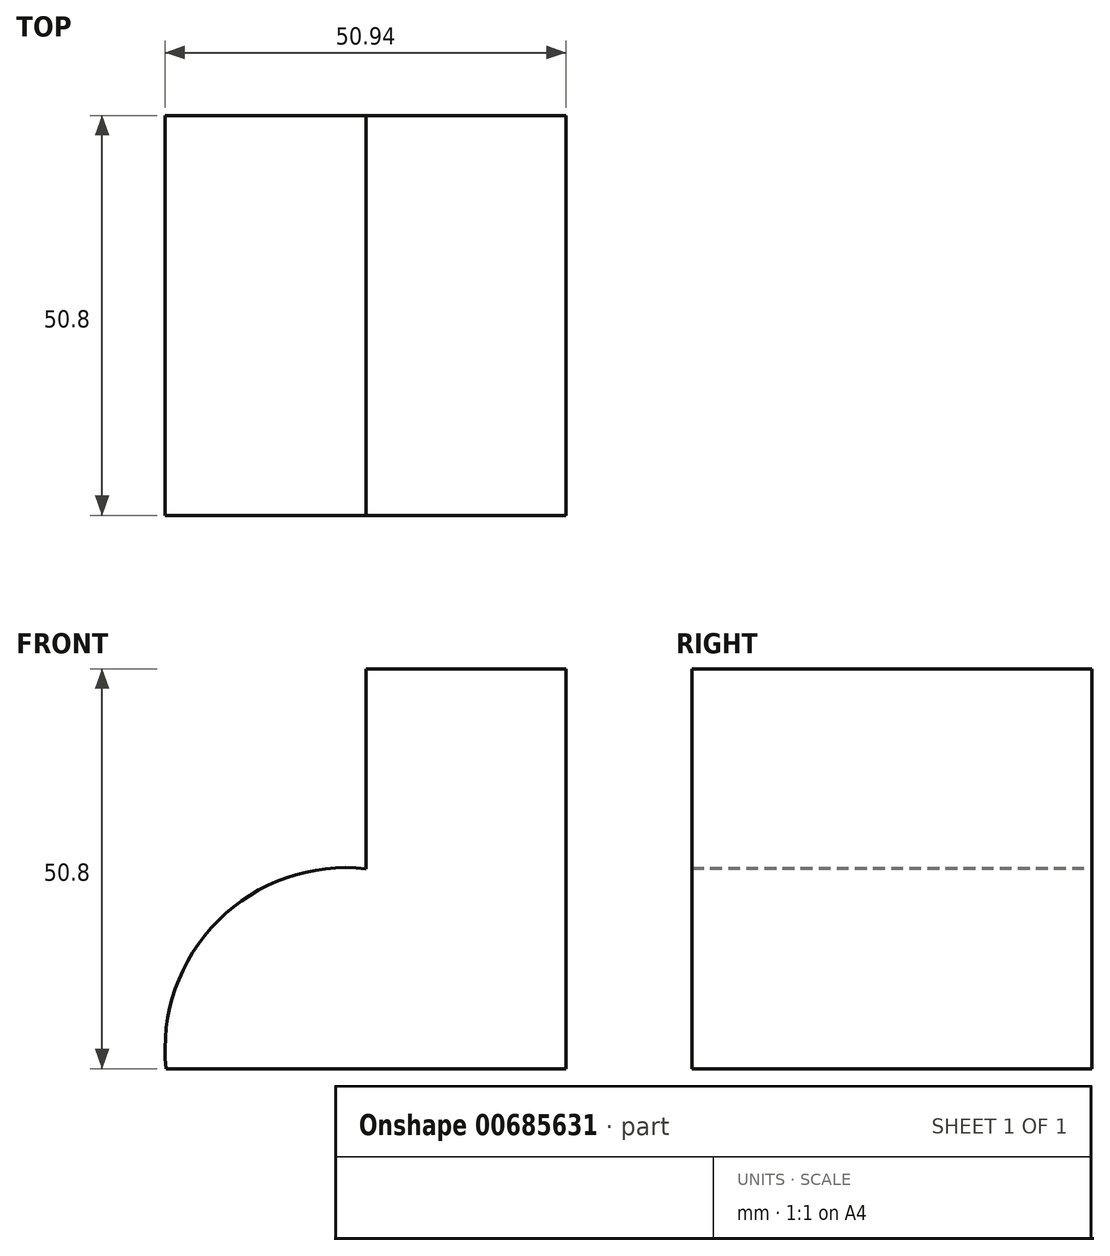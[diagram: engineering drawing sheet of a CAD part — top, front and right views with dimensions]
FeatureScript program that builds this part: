
annotation { "Feature Type Name" : "Feature", "Feature Type Description" : "" }
export const myFeature = defineFeature(function(context is Context, id is Id, definition is map)
    precondition{}
    {
        {
            var Q0;
            Q0=qCreatedBy(makeId("Front.planeOp"),FACE);
            var sketch = newSketch(context, id + "F0", { "sketchPlane" : qUnion([Q0])});
            skLineSegment(sketch, "E0", {"start": v(36.72, 23.26) * mm, "end": v(36.72, -27.54) * mm});
            skLineSegment(sketch, "E1", {"start": v(36.72, -27.54) * mm, "end": v(-14.08, -27.54) * mm});
            skLineSegment(sketch, "E2", {"start": v(36.72, 23.26) * mm, "end": v(11.32, 23.26) * mm});
            skLineSegment(sketch, "E3", {"start": v(11.32, 23.26) * mm, "end": v(11.32, -2.14) * mm});
            skArc(sketch, "E4", {"start": v(11.32, -2.14) * mm, "mid": v(-7.48, -8.74) * mm, "end": v(-14.08, -27.54) * mm});
            skSolve(sketch);
        }
        {
            var Q0;
            Q0 = qSketchRegion(id + "F0", true);
            extrude(context, id + "F1", {"entities" : qUnion([Q0]), "depth" : 50.8 * mm, "offsetDistance" : 25.4 * mm});
        }
    });
